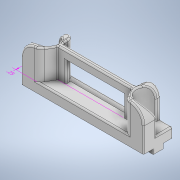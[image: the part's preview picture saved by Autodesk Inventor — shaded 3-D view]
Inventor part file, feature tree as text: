
AUTODESK INVENTOR PART (.ipt)
format: ipt  version: 2020 (Build 240168000, 168)  size: 444,416 bytes
history: native  units: in
note: dims shown in document units (in); Inventor stores cm internally (conversion verified against a paired STEP export)
features: fillet x8, sketch x6, extrude x5, other x2, hole x1
ambient origin geometry x8: Origin, YZ Plane, XZ Plane, XY Plane, X Axis, Y Axis, Z Axis, Center Point
bodies: Solid1 (feature_tree)
feature tree (22):
  other  "Annotations"
  extrude  "Extrusion1"  Depth=0.6in
  extrude  "Extrusion5"  Depth=0.1in
  extrude  "Extrusion8"  Depth=2.5in
  hole  "Hole3"  [1 undecoded]
  extrude  "Extrusion9"  Depth=0.5in
  extrude  "Extrusion10"  Depth=0.1in
  fillet  "Fillet4"  Radius=0.25in
  fillet  "Fillet5"  Radius=0.6in
  fillet  "Fillet6"  [1 undecoded]
  fillet  "Fillet7"  [1 undecoded]
  fillet  "Fillet8"  Radius=0.16in
  fillet  "Fillet9"  Radius=1.18in
  fillet  "Fillet10"  Radius=0.44in
  fillet  "Fillet11"  Radius=0.1in
  sketch  "Sketch1"  dims[d0=2.5in d1=0.6in]
  sketch  "Sketch6"  dims[d2=0.2in d3=0.0in d27=0.1in]
  sketch  "Sketch13"  dims[d28=0.2in d29=2.5in]
  sketch  "Sketch15"  dims[d30=0.2in d31=0.1in d32=0.0in]
  sketch  "Sketch16"  dims[d61=0.5in d62=0.5in]
  sketch  "Sketch18"  dims[d63=0.05in d64=0.1in d65=0.25in d66=0.6in d67=0.0in d68=60.0deg d69=120.0deg d70=0.2in d71=0.75in d72=0.4in d73=0.6in d74=0.5635in d75=1.0in d76=0.8108in d77=0.16in d78=1.18in d79=0.44in d80=0.1in d81=0.0in d89=0.12in d90=0.25in d91=0.0in d93=0.03in d94=0.15in d95=0.3in d96=0.2in d97=0.03in d98=0.03in d99=0.03in d100=0.03in d86=0.069in d87=0.3069in d88=0.25in d14=1.0in d15=1.0in d16=1.0in d17=0.15in d18=0.25in d19=0.375in d20=0.5635in d21=0.75in d22=0.8108in d23=0.0625in d24=0.75in d25=0.375in d92=0.0344in]
  other  "Linear Dimension 1"
note: 3 required parameter values undecoded (feature->parameter linkage not recoverable at this tier; creation-order binding heuristic only, values carry confidence <= 0.55)
